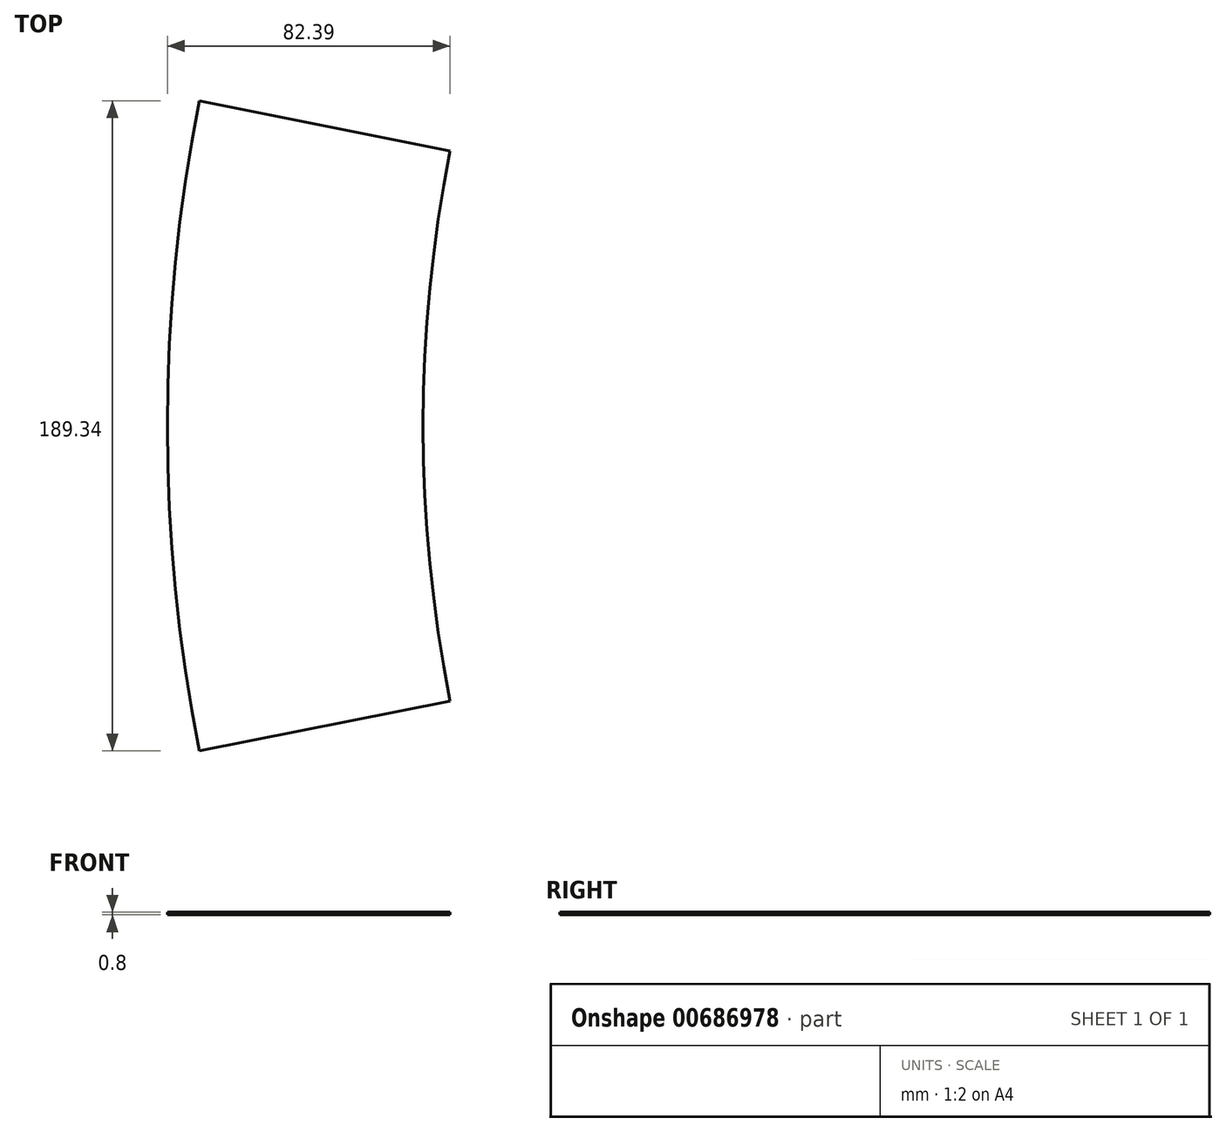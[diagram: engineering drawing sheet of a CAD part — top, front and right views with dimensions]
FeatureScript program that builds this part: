
annotation { "Feature Type Name" : "Feature", "Feature Type Description" : "" }
export const myFeature = defineFeature(function(context is Context, id is Id, definition is map)
    precondition{}
    {
        {
            var Q0;
            Q0=qCreatedBy(makeId("Top.planeOp"),FACE);
            var sketch = newSketch(context, id + "F0", { "sketchPlane" : qUnion([Q0])});
            skArc(sketch, "E0", {"start": v(50.07, 94.67) * mm, "mid": v(40.75, 0) * mm, "end": v(50.07, -94.67) * mm});
            skArc(sketch, "E1", {"start": v(123.14, 80.13) * mm, "mid": v(115.25, 0) * mm, "end": v(123.14, -80.13) * mm});
            skLineSegment(sketch, "E2", {"start": v(50.07, 94.67) * mm, "end": v(123.14, 80.13) * mm});
            skLineSegment(sketch, "E3", {"start": v(123.14, -80.13) * mm, "end": v(50.07, -94.67) * mm});
            skLineSegment(sketch, "E4", {"start": v(123.14, 80.13) * mm, "end": v(526, 0) * mm});
            skLineSegment(sketch, "E5", {"start": v(123.14, -80.13) * mm, "end": v(526, 0) * mm});
            skSolve(sketch);
        }
        {
            var Q0;
            Q0=makeQuery(id+"F0.imprint","IMPRINT",FACE,{"disambiguationData":[TD([[makeQuery(id+"F0.imprint","IMPRINT",EDGE,{"derivedFrom":sQuery(id+"F0.wireOp",EDGE,"E0")}),1.0]])]});
            extrude(context, id + "F1", {"entities" : qUnion([Q0]), "depth" : .8 * mm, "offsetDistance" : 25 * mm});
        }
    });
